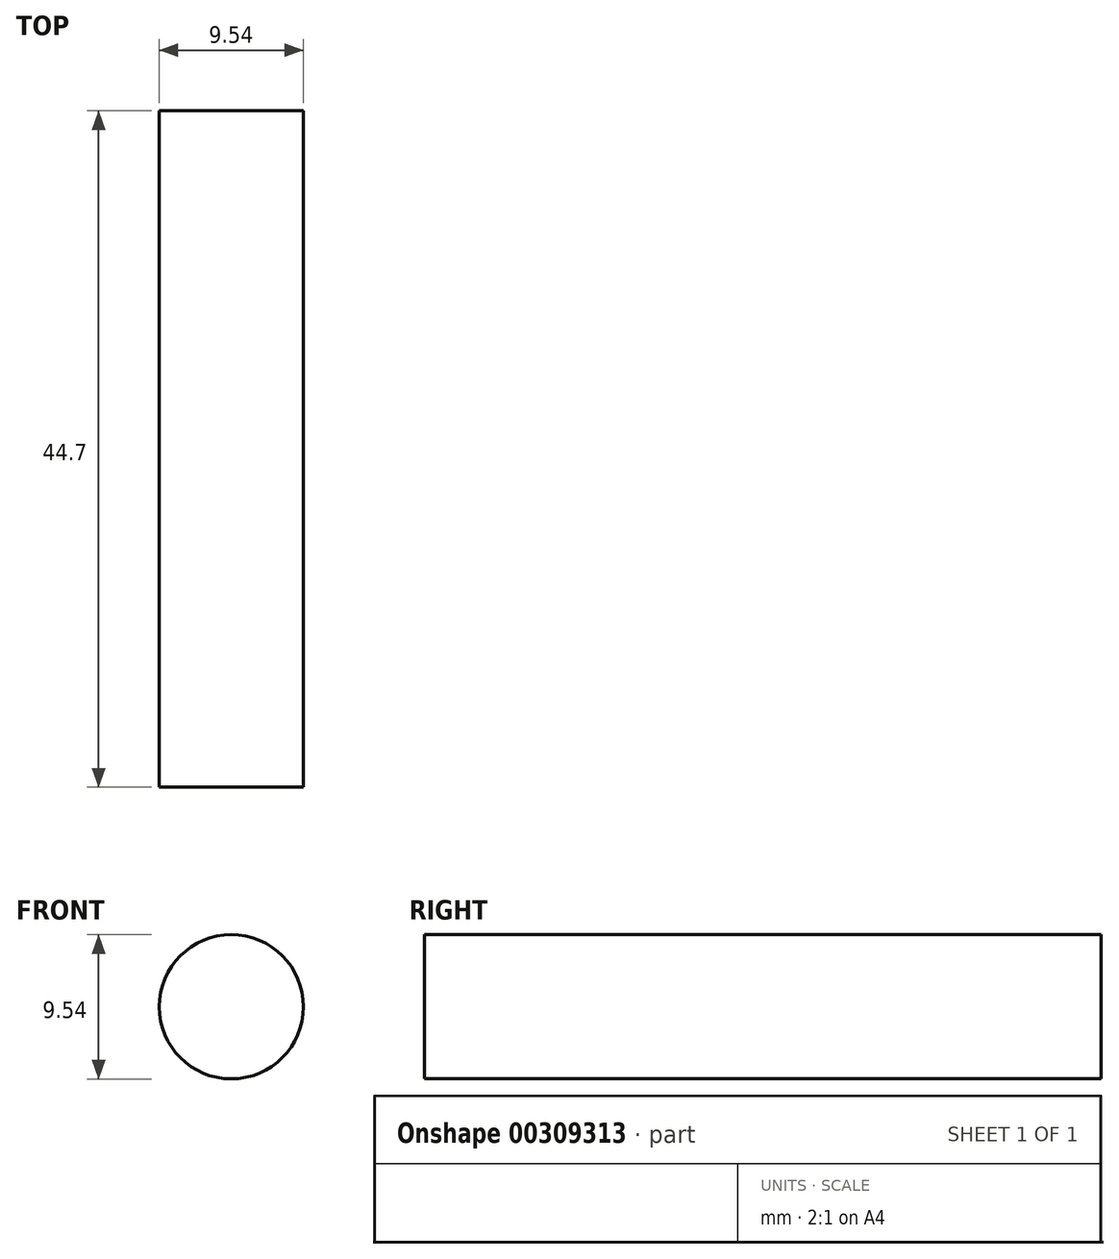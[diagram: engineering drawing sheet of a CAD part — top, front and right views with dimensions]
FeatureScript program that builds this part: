
annotation { "Feature Type Name" : "Feature", "Feature Type Description" : "" }
export const myFeature = defineFeature(function(context is Context, id is Id, definition is map)
    precondition{}
    {
        {
            var Q0;
            Q0=qCreatedBy(makeId("Front.planeOp"),FACE);
            var sketch = newSketch(context, id + "F0", { "sketchPlane" : qUnion([Q0])});
            skCircle(sketch, "E0", {"center": v(0, 0) * mm, "radius": 4.76 * mm});
            skSolve(sketch);
        }
        {
            var Q0;
            Q0=makeQuery(id+"F0.imprint","IMPRINT",FACE,{"disambiguationData":[TD([[makeQuery(id+"F0.imprint","IMPRINT",EDGE,{"derivedFrom":sQuery(id+"F0.wireOp",EDGE,"E0")}),1.0]])]});
            extrude(context, id + "F1", {"entities" : qUnion([Q0]), "oppositeDirection" : true, "depth" : 44.7 * mm});
        }
    });
